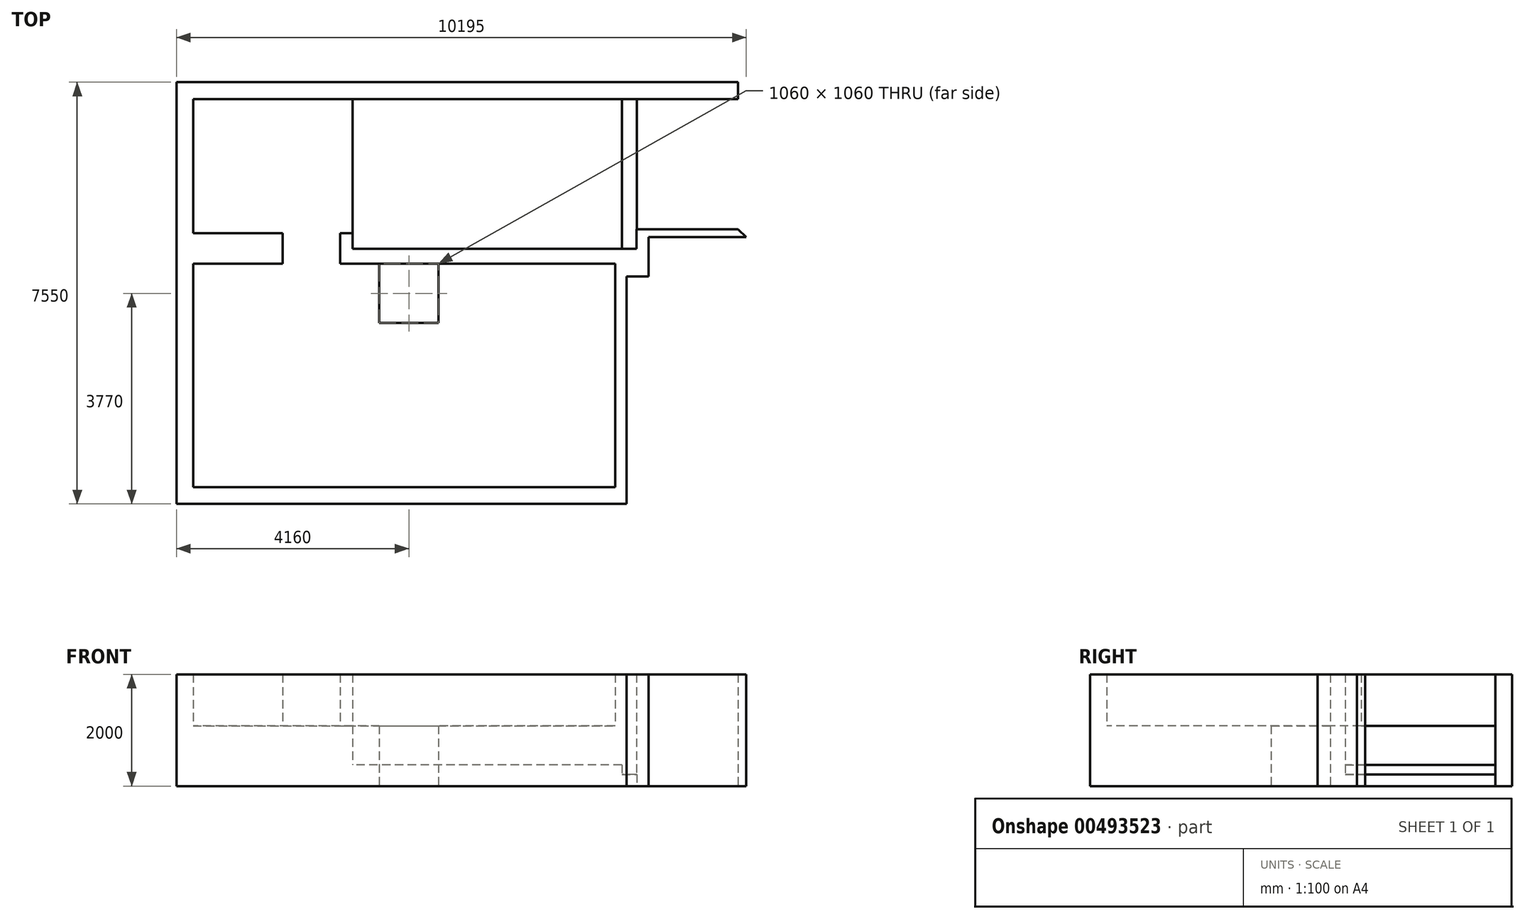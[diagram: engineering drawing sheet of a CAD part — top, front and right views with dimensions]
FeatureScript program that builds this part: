
annotation { "Feature Type Name" : "Feature", "Feature Type Description" : "" }
export const myFeature = defineFeature(function(context is Context, id is Id, definition is map)
    precondition{}
    {
        {
            var Q0;
            Q0=qCreatedBy(makeId("Top.planeOp"),FACE);
            var sketch = newSketch(context, id + "F0", { "sketchPlane" : qUnion([Q0])});
            skLineSegment(sketch, "E0", {"start": v(-12921.96, 6101.99) * mm, "end": v(-12921.96, 3701.99) * mm});
            skLineSegment(sketch, "E1", {"start": v(-12921.96, 3701.99) * mm, "end": v(-12921.96, 3151.99) * mm});
            skLineSegment(sketch, "E2", {"start": v(-12921.96, 3151.99) * mm, "end": v(-12921.96, -848.01) * mm});
            skLineSegment(sketch, "E3", {"start": v(-12921.96, -848.01) * mm, "end": v(-5371.96, -848.01) * mm});
            skLineSegment(sketch, "E4", {"start": v(-5371.96, -848.01) * mm, "end": v(-5371.96, 3151.99) * mm});
            skLineSegment(sketch, "E5", {"start": v(-5371.96, 3151.99) * mm, "end": v(-10291.96, 3151.99) * mm});
            skLineSegment(sketch, "E6", {"start": v(-10291.96, 3151.99) * mm, "end": v(-10291.96, 3701.99) * mm});
            skLineSegment(sketch, "E7", {"start": v(-10291.96, 3701.99) * mm, "end": v(-10071.96, 3701.99) * mm});
            skLineSegment(sketch, "E8", {"start": v(-10071.96, 3701.99) * mm, "end": v(-10071.96, 3421.99) * mm});
            skLineSegment(sketch, "E9", {"start": v(-10071.96, 3421.99) * mm, "end": v(-4986.96, 3421.99) * mm});
            skLineSegment(sketch, "E10", {"start": v(-4986.96, 3421.99) * mm, "end": v(-4986.96, 3771.99) * mm});
            skLineSegment(sketch, "E11", {"start": v(-4986.96, 3771.99) * mm, "end": v(-3171.96, 3771.99) * mm});
            skLineSegment(sketch, "E12", {"start": v(-3171.96, 3771.99) * mm, "end": v(-3171.96, 5011.99) * mm});
            skLineSegment(sketch, "E13", {"start": v(-3171.96, 5011.99) * mm, "end": v(-3171.96, 5861.99) * mm});
            skLineSegment(sketch, "E14", {"start": v(-3171.96, 5861.99) * mm, "end": v(-3171.96, 6101.99) * mm});
            skLineSegment(sketch, "E15", {"start": v(-3171.96, 6101.99) * mm, "end": v(-12921.96, 6101.99) * mm});
            skLineSegment(sketch, "E16", {"start": v(-12921.96, 3701.99) * mm, "end": v(-11321.96, 3701.99) * mm});
            skLineSegment(sketch, "E17", {"start": v(-11321.96, 3701.99) * mm, "end": v(-11321.96, 3151.99) * mm});
            skLineSegment(sketch, "E18", {"start": v(-11321.96, 3151.99) * mm, "end": v(-12921.96, 3151.99) * mm});
            skLineSegment(sketch, "E19", {"start": v(-9591.96, 3151.99) * mm, "end": v(-9591.96, 2091.99) * mm});
            skLineSegment(sketch, "E20", {"start": v(-9591.96, 2091.99) * mm, "end": v(-8531.96, 2091.99) * mm});
            skLineSegment(sketch, "E21", {"start": v(-8531.96, 2091.99) * mm, "end": v(-8531.96, 3151.99) * mm});
            skLineSegment(sketch, "E22", {"start": v(-3171.96, 6101.99) * mm, "end": v(-3026.96, 6101.99) * mm});
            skSolve(sketch);
        }
        {
            var Q0;
            Q0=makeQuery(id+"F0.imprint","IMPRINT",FACE,{"disambiguationData":[TD([[makeQuery(id+"F0.imprint","IMPRINT",EDGE,{"derivedFrom":sQuery(id+"F0.wireOp",EDGE,"E0")}),1.0]])]});
            var sketch = newSketch(context, id + "F1", { "sketchPlane" : qUnion([Q0])});
            skLineSegment(sketch, "E23.0", {"start": v(-3171.96, 6101.99) * mm, "end": v(-12921.96, 6101.99) * mm});
            skLineSegment(sketch, "E24", {"start": v(-12921.96, 6101.99) * mm, "end": v(-12921.96, 6401.99) * mm});
            skLineSegment(sketch, "E25", {"start": v(-12921.96, 6401.99) * mm, "end": v(-3171.96, 6401.99) * mm});
            skLineSegment(sketch, "E26", {"start": v(-3171.96, 6401.99) * mm, "end": v(-3171.96, 6101.99) * mm});
            skLineSegment(sketch, "E27.0", {"start": v(-12921.96, 3701.99) * mm, "end": v(-11321.96, 3701.99) * mm});
            skLineSegment(sketch, "E28.0", {"start": v(-11321.96, 3701.99) * mm, "end": v(-11321.96, 3151.99) * mm});
            skLineSegment(sketch, "E29.0", {"start": v(-11321.96, 3151.99) * mm, "end": v(-12921.96, 3151.99) * mm});
            skLineSegment(sketch, "E30", {"start": v(-12921.96, 6401.99) * mm, "end": v(-12921.96, 3701.99) * mm});
            skLineSegment(sketch, "E31", {"start": v(-12921.96, 3151.99) * mm, "end": v(-12921.96, -1148.01) * mm});
            skLineSegment(sketch, "E32", {"start": v(-12921.96, -1148.01) * mm, "end": v(-13221.96, -1148.01) * mm});
            skLineSegment(sketch, "E33", {"start": v(-13221.96, -1148.01) * mm, "end": v(-13221.96, 6401.99) * mm});
            skLineSegment(sketch, "E34", {"start": v(-13221.96, 6401.99) * mm, "end": v(-12921.96, 6401.99) * mm});
            skLineSegment(sketch, "E35.0", {"start": v(-3171.96, 6101.99) * mm, "end": v(-3026.96, 6101.99) * mm});
            skLineSegment(sketch, "E36", {"start": v(-3171.96, 6401.99) * mm, "end": v(-3026.96, 6401.99) * mm});
            skLineSegment(sketch, "E37", {"start": v(-3026.96, 6401.99) * mm, "end": v(-3026.96, 6101.99) * mm});
            skLineSegment(sketch, "E38", {"start": v(-3026.96, 6101.99) * mm, "end": v(-3026.96, 3626.99) * mm});
            skLineSegment(sketch, "E39", {"start": v(-3026.96, 3626.99) * mm, "end": v(-4772.85, 3626.99) * mm});
            skLineSegment(sketch, "E40", {"start": v(-4772.85, 3626.99) * mm, "end": v(-4772.85, 2925.8) * mm});
            skLineSegment(sketch, "E41", {"start": v(-4772.85, 2925.8) * mm, "end": v(-5164.04, 2925.8) * mm});
            skLineSegment(sketch, "E42", {"start": v(-5164.04, 2925.8) * mm, "end": v(-5164.04, -1148.01) * mm});
            skLineSegment(sketch, "E43", {"start": v(-5164.04, -1148.01) * mm, "end": v(-12921.96, -1148.01) * mm});
            skLineSegment(sketch, "E44.0", {"start": v(-4986.96, 3771.99) * mm, "end": v(-3171.96, 3771.99) * mm});
            skLineSegment(sketch, "E45", {"start": v(-3171.96, 3771.99) * mm, "end": v(-3171.96, 6101.99) * mm});
            skLineSegment(sketch, "E46.0", {"start": v(-12921.96, -848.01) * mm, "end": v(-5371.96, -848.01) * mm});
            skLineSegment(sketch, "E47.0", {"start": v(-10071.96, 3421.99) * mm, "end": v(-4986.96, 3421.99) * mm});
            skLineSegment(sketch, "E48.0", {"start": v(-10291.96, 3151.99) * mm, "end": v(-10291.96, 3701.99) * mm});
            skLineSegment(sketch, "E49.0", {"start": v(-5371.96, 3151.99) * mm, "end": v(-10291.96, 3151.99) * mm});
            skLineSegment(sketch, "E50.0", {"start": v(-5371.96, -848.01) * mm, "end": v(-5371.96, 3151.99) * mm});
            skLineSegment(sketch, "E51.0", {"start": v(-10071.96, 3701.99) * mm, "end": v(-10071.96, 3421.99) * mm});
            skLineSegment(sketch, "E52.0", {"start": v(-10291.96, 3701.99) * mm, "end": v(-10071.96, 3701.99) * mm});
            skLineSegment(sketch, "E53.0", {"start": v(-4986.96, 3421.99) * mm, "end": v(-4986.96, 3771.99) * mm});
            skLineSegment(sketch, "E54", {"start": v(-3171.96, 3771.99) * mm, "end": v(-3026.96, 3626.99) * mm});
            skLineSegment(sketch, "E55", {"start": v(-5371.96, -848.01) * mm, "end": v(-5164.04, -1148.01) * mm});
            skSolve(sketch);
        }
        {
            var Q0;
            Q0=makeQuery(id+"F0.imprint","IMPRINT",FACE,{"disambiguationData":[TD([[makeQuery(id+"F0.imprint","IMPRINT",EDGE,{"derivedFrom":sQuery(id+"F0.wireOp",EDGE,"E0")}),1.0]])]});
            var sketch = newSketch(context, id + "F2", { "sketchPlane" : qUnion([Q0])});
            skLineSegment(sketch, "E56.0", {"start": v(-3171.96, 6101.99) * mm, "end": v(-12921.96, 6101.99) * mm});
            skLineSegment(sketch, "E57.0", {"start": v(-12921.96, 3701.99) * mm, "end": v(-11321.96, 3701.99) * mm});
            skLineSegment(sketch, "E58", {"start": v(-12921.96, 6101.99) * mm, "end": v(-12921.96, 3701.99) * mm});
            skLineSegment(sketch, "E59.0", {"start": v(-3171.96, 3771.99) * mm, "end": v(-3171.96, 6101.99) * mm});
            skLineSegment(sketch, "E60", {"start": v(-4981.96, 6101.99) * mm, "end": v(-4981.96, 3771.99) * mm});
            skLineSegment(sketch, "E61.0", {"start": v(-10071.96, 3421.99) * mm, "end": v(-4986.96, 3421.99) * mm});
            skLineSegment(sketch, "E62", {"start": v(-5251.96, 6101.99) * mm, "end": v(-5251.96, 3421.99) * mm});
            skLineSegment(sketch, "E63.0", {"start": v(-10291.96, 3701.99) * mm, "end": v(-10071.96, 3701.99) * mm});
            skLineSegment(sketch, "E64", {"start": v(-10071.96, 3701.99) * mm, "end": v(-10071.96, 6101.99) * mm});
            skLineSegment(sketch, "E65.0", {"start": v(-11321.96, 3701.99) * mm, "end": v(-11321.96, 3151.99) * mm});
            skLineSegment(sketch, "E66.0", {"start": v(-11321.96, 3151.99) * mm, "end": v(-12921.96, 3151.99) * mm});
            skLineSegment(sketch, "E67.0", {"start": v(-12921.96, 3151.99) * mm, "end": v(-12921.96, -848.01) * mm});
            skLineSegment(sketch, "E68.0", {"start": v(-12921.96, -848.01) * mm, "end": v(-5371.96, -848.01) * mm});
            skLineSegment(sketch, "E69.0", {"start": v(-5371.96, -848.01) * mm, "end": v(-5371.96, 3151.99) * mm});
            skLineSegment(sketch, "E70.0", {"start": v(-5371.96, 3151.99) * mm, "end": v(-10291.96, 3151.99) * mm});
            skLineSegment(sketch, "E71.0", {"start": v(-10291.96, 3151.99) * mm, "end": v(-10291.96, 3701.99) * mm});
            skLineSegment(sketch, "E72", {"start": v(-10071.96, 3701.99) * mm, "end": v(-10071.96, 3421.99) * mm});
            skLineSegment(sketch, "E73", {"start": v(-4981.96, 3771.99) * mm, "end": v(-4986.96, 3421.99) * mm});
            skSolve(sketch);
        }
        {
            var Q0;
            {var subQ1=sQuery(id+"F2.wireOp",EDGE,"E60");Q0=makeQuery(id+"F2.imprint","IMPRINT",FACE,{"disambiguationData":[TD([[makeQuery(id+"F2.imprint","IMPRINT",EDGE,{"derivedFrom":subQ1}),-1.0]])]});}
            extrude(context, id + "F3", {"entities" : qUnion([Q0]), "depth" : 210 * mm});
        }
        {
            var Q0;
            {var subQ3=sQuery(id+"F2.wireOp",EDGE,"E62");Q0=makeQuery(id+"F2.imprint","IMPRINT",FACE,{"disambiguationData":[TD([[makeQuery(id+"F2.imprint","IMPRINT",EDGE,{"derivedFrom":subQ3}),-1.0]])]});}
            extrude(context, id + "F4", {"entities" : qUnion([Q0]), "operationType" : NewBodyOperationType.ADD, "depth" : 380 * mm});
        }
        {
            var Q0;
            Q0=makeQuery(id+"F2.imprint","IMPRINT",FACE,{"disambiguationData":[TD([[makeQuery(id+"F2.imprint","IMPRINT",EDGE,{"derivedFrom":sQuery(id+"F2.wireOp",EDGE,"E57.0")}),1.0]])]});
            extrude(context, id + "F5", {"entities" : qUnion([Q0]), "operationType" : NewBodyOperationType.ADD, "depth" : 1080 * mm});
        }
        {
            var Q0;
            {var subQ0=sQuery(id+"F1.wireOp",EDGE,"E23.0");Q0=makeQuery(id+"F1.imprint","IMPRINT",FACE,{"disambiguationData":[TD([[makeQuery(id+"F1.imprint","IMPRINT",EDGE,{"derivedFrom":subQ0}),-1.0]])]});}
            extrude(context, id + "F6", {"entities" : qUnion([Q0]), "operationType" : NewBodyOperationType.ADD, "depth" : 2000 * mm});
        }
        {
            var Q0;
            Q0=makeQuery(id+"F1.imprint","IMPRINT",FACE,{"disambiguationData":[TD([[makeQuery(id+"F1.imprint","IMPRINT",EDGE,{"derivedFrom":sQuery(id+"F1.wireOp",EDGE,"E39")}),-1.0]])]});
            extrude(context, id + "F7", {"entities" : qUnion([Q0]), "operationType" : NewBodyOperationType.ADD, "depth" : 2000 * mm});
        }
        {
            var Q0;
            {var subQ4=sQuery(id+"F1.wireOp",EDGE,"E27.0");Q0=makeQuery(id+"F1.imprint","IMPRINT",FACE,{"disambiguationData":[TD([[makeQuery(id+"F1.imprint","IMPRINT",EDGE,{"derivedFrom":subQ4}),-1.0]])]});}
            extrude(context, id + "F8", {"entities" : qUnion([Q0]), "operationType" : NewBodyOperationType.ADD, "depth" : 2000 * mm});
        }
        {
            var Q0;
            {var subQ2=sQuery(id+"F1.wireOp",EDGE,"E43");Q0=makeQuery(id+"F1.imprint","IMPRINT",FACE,{"disambiguationData":[TD([[makeQuery(id+"F1.imprint","IMPRINT",EDGE,{"derivedFrom":subQ2}),-1.0]])]});}
            extrude(context, id + "F9", {"entities" : qUnion([Q0]), "operationType" : NewBodyOperationType.ADD, "depth" : 2000 * mm});
        }
        {
            var Q0;
            Q0=makeQuery(id+"F3.opExtrude","SWEPT_BODY",BODY,{"disambiguationData":[OSD([sQuery(id+"F0.wireOp",EDGE,"E10"),sQuery(id+"F0.wireOp",EDGE,"E11"),sQuery(id+"F2.wireOp",EDGE,"E56.0"),sQuery(id+"F2.wireOp",EDGE,"E60"),sQuery(id+"F2.wireOp",EDGE,"E61.0"),sQuery(id+"F2.wireOp",EDGE,"E62")])]});
            transform(context, id + "F10", {"entities" : qUnion([Q0]), "transformType" : TransformType.TRANSLATION_3D, "dx" : 0 * mm, "dy" : 0 * mm, "dz" : 0 * mm, "makeCopy" : true});
        }
    });
